# Revit family: 110402-00001 Плита разгрузочная для ККСр-3 ОП-1-У
name_source: partatom
category: Обобщенные модели
units: mm (PartAtom-declared; Revit-internal decimal feet)

## family parameters
Всегда вертикально = Да
Может служить основой для арматурных стержней = Нет
На основе рабочей плоскости = Нет
Общий = Нет
При загрузке вырезать с полостями = Нет
Размер круглого соединителя = Использовать диаметр
Тип детали = Нормальный
Точка расчета площади = Нет

## types (2) — shared parameters
ADSK_Изготовитель = АО СВЯЗЬСТРОЙДЕТАЛЬ
ADSK_Масса = 1570
ADSK_Сертификат соответствия = https://www.ssd.ru
ADSK_Ссылка на сайт = https://www.ssd.ru

## per-type parameters (varying)
| type | ADSK_Код изделия | ADSK_Марка | ADSK_Марка бетона | ADSK_Наименование |
| Плита разгрузочная для ККСр-1,ККСр-2 "ОП-1к-У" | 110402-00001 | ККСр-3 "ОП-1-У" | В20 | Плита разгрузочная для ККСр-3 "ОП-1-У" |
| Плита разгрузочная для ККСр-3 "ОП-1-У" (В25) | 110402-00097 | ККСр-3 "ОП-1-У" (В25) | В25 | Плита разгрузочная для ККСр-3 "ОП-1-У" (В25) |
